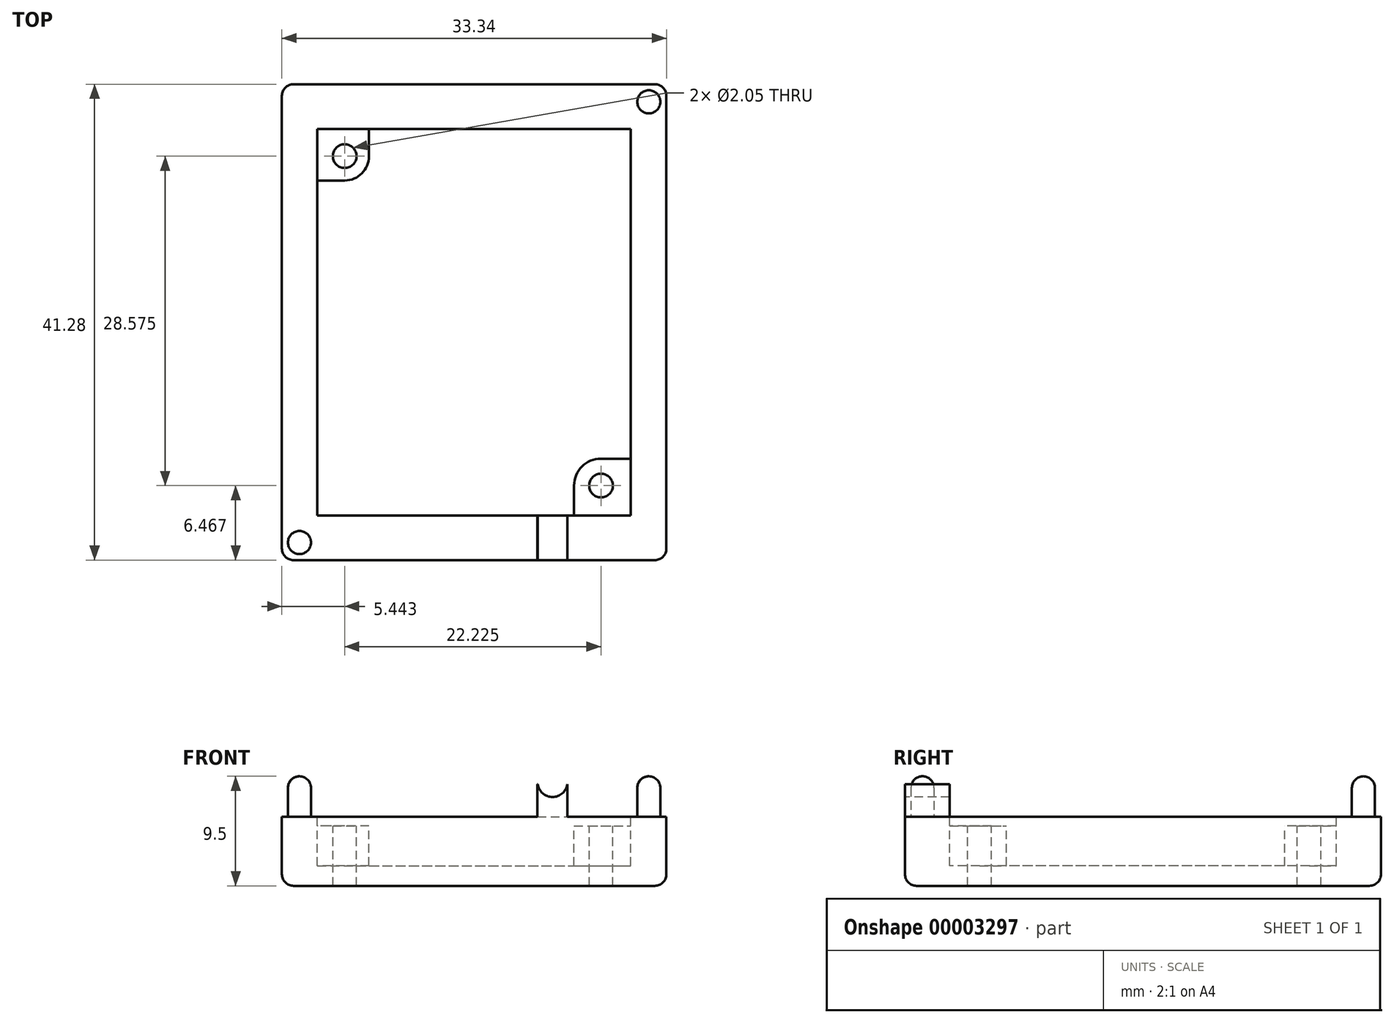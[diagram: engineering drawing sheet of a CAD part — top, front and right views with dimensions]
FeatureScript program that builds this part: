
annotation { "Feature Type Name" : "Feature", "Feature Type Description" : "" }
export const myFeature = defineFeature(function(context is Context, id is Id, definition is map)
    precondition{}
    {
        {
            var Q0;
            Q0=qCreatedBy(makeId("Top.planeOp"),FACE);
            var sketch = newSketch(context, id + "F0", { "sketchPlane" : qUnion([Q0])});
            skLineSegment(sketch, "E0.rect.bottom", {"start": v(16.67, 20.64) * mm, "end": v(-16.67, 20.64) * mm});
            skLineSegment(sketch, "E0.rect.top", {"start": v(16.67, -20.64) * mm, "end": v(-16.67, -20.64) * mm});
            skLineSegment(sketch, "E0.rect.left", {"start": v(16.67, 20.64) * mm, "end": v(16.67, -20.64) * mm});
            skLineSegment(sketch, "E0.rect.right", {"start": v(-16.67, 20.64) * mm, "end": v(-16.67, -20.64) * mm});
            skPoint(sketch, "E0.rect.middle", {"position": v(0, 0) * mm});
            skSolve(sketch);
        }
        {
            var Q0;
            Q0=makeQuery(id+"F0.imprint","IMPRINT",FACE,{"disambiguationData":[TD([[makeQuery(id+"F0.imprint","IMPRINT",EDGE,{"derivedFrom":sQuery(id+"F0.wireOp",EDGE,"E0.rect.bottom")}),1.0]])]});
            extrude(context, id + "F1", {"entities" : qUnion([Q0]), "oppositeDirection" : true, "depth" : 6 * mm});
        }
        {
            var Q0;
            Q0=makeQuery(id+"F1.opExtrude","CAP_FACE",FACE,{"disambiguationData":[OSD([sQuery(id+"F0.wireOp",EDGE,"E0.rect.bottom"),sQuery(id+"F0.wireOp",EDGE,"E0.rect.top"),sQuery(id+"F0.wireOp",EDGE,"E0.rect.left"),sQuery(id+"F0.wireOp",EDGE,"E0.rect.right")])],"isStart":true});
            var sketch = newSketch(context, id + "F2", { "sketchPlane" : qUnion([Q0])});
            skLineSegment(sketch, "E1.rect.bottom", {"start": v(13.33, 16.51) * mm, "end": v(-13.34, 16.51) * mm});
            skLineSegment(sketch, "E1.rect.top", {"start": v(13.34, -16.51) * mm, "end": v(-13.33, -16.51) * mm});
            skLineSegment(sketch, "E1.rect.left", {"start": v(13.33, 16.51) * mm, "end": v(13.34, -16.51) * mm});
            skLineSegment(sketch, "E1.rect.right", {"start": v(-13.34, 16.51) * mm, "end": v(-13.33, -16.51) * mm});
            skPoint(sketch, "E1.rect.middle", {"position": v(0, 0) * mm});
            skCircle(sketch, "E2", {"center": v(11.23, 14.4) * mm, "radius": 1.25 * mm});
            skCircle(sketch, "E3", {"center": v(-11, -14.17) * mm, "radius": 1.25 * mm});
            skCircle(sketch, "E4", {"center": v(11.23, 14.4) * mm, "radius": 2.1 * mm});
            skCircle(sketch, "E5", {"center": v(-11, -14.17) * mm, "radius": 2.34 * mm});
            skLineSegment(sketch, "E6.0", {"start": v(13.59, 16.76) * mm, "end": v(-13.59, 16.76) * mm});
            skLineSegment(sketch, "E6.1", {"start": v(13.59, 16.76) * mm, "end": v(13.59, -16.76) * mm});
            skLineSegment(sketch, "E6.2", {"start": v(13.59, -16.76) * mm, "end": v(-13.59, -16.76) * mm});
            skLineSegment(sketch, "E6.3", {"start": v(-13.59, 16.76) * mm, "end": v(-13.59, -16.76) * mm});
            skLineSegment(sketch, "E7", {"start": v(9.12, 14.4) * mm, "end": v(9.12, 16.76) * mm});
            skLineSegment(sketch, "E8", {"start": v(11.23, 12.3) * mm, "end": v(13.59, 12.3) * mm});
            skLineSegment(sketch, "E9", {"start": v(-11, -11.84) * mm, "end": v(-13.59, -11.84) * mm});
            skLineSegment(sketch, "E10", {"start": v(-8.66, -14.17) * mm, "end": v(-8.66, -16.76) * mm});
            skSolve(sketch);
        }
        {
            var Q0;
            {var subQ6=sQuery(id+"F2.wireOp",EDGE,"E1.rect.right");var subQ10=sQuery(id+"F2.wireOp",EDGE,"E1.rect.bottom");var subQ18=makeQuery(id+"F2.imprint","INTERSECT",VERTEX,{"derivedFrom":[subQ10,subQ6]});Q0=makeQuery(id+"F2.imprint","IMPRINT",FACE,{"disambiguationData":[TD([[makeQuery(id+"F2.imprint","IMPRINT",EDGE,{"disambiguationData":[TD([[subQ18,1.0]])],"derivedFrom":subQ10}),1.0]])]});}
            var Q1;
            {var subQ1=sQuery(id+"F2.wireOp",EDGE,"E1.rect.right");var subQ6=sQuery(id+"F2.wireOp",EDGE,"E1.rect.bottom");var subQ11=makeQuery(id+"F2.imprint","INTERSECT",VERTEX,{"derivedFrom":[subQ6,subQ1]});Q1=makeQuery(id+"F2.imprint","IMPRINT",FACE,{"disambiguationData":[TD([[makeQuery(id+"F2.imprint","IMPRINT",EDGE,{"disambiguationData":[TD([[subQ11,1.0]])],"derivedFrom":subQ6}),-1.0]])]});}
            var Q2;
            {var subQ1=sQuery(id+"F2.wireOp",EDGE,"E1.rect.left");var subQ6=sQuery(id+"F2.wireOp",EDGE,"E1.rect.top");var subQ11=makeQuery(id+"F2.imprint","INTERSECT",VERTEX,{"derivedFrom":[subQ6,subQ1]});Q2=makeQuery(id+"F2.imprint","IMPRINT",FACE,{"disambiguationData":[TD([[makeQuery(id+"F2.imprint","IMPRINT",EDGE,{"disambiguationData":[TD([[subQ11,-1.0]])],"derivedFrom":subQ6}),1.0]])]});}
            extrude(context, id + "F3", {"entities" : qUnion([Q0, Q1, Q2]), "operationType" : NewBodyOperationType.REMOVE, "oppositeDirection" : true, "depth" : 4.26 * mm});
        }
        {
            var Q0;
            Q0=makeQuery(id+"F1.opExtrude","CAP_FACE",FACE,{"disambiguationData":[OSD([sQuery(id+"F0.wireOp",EDGE,"E0.rect.bottom"),sQuery(id+"F0.wireOp",EDGE,"E0.rect.top"),sQuery(id+"F0.wireOp",EDGE,"E0.rect.left"),sQuery(id+"F0.wireOp",EDGE,"E0.rect.right")])],"isStart":true});
            var sketch = newSketch(context, id + "F4", { "sketchPlane" : qUnion([Q0])});
            skLineSegment(sketch, "E11", {"start": v(9.12, 16.76) * mm, "end": v(13.59, 16.76) * mm});
            skLineSegment(sketch, "E12", {"start": v(13.59, 16.76) * mm, "end": v(13.59, 12.3) * mm});
            skLineSegment(sketch, "E13", {"start": v(13.59, 12.3) * mm, "end": v(11.23, 12.3) * mm});
            skArc(sketch, "E14", {"start": v(9.12, 14.4) * mm, "mid": v(9.74, 12.91) * mm, "end": v(11.23, 12.3) * mm});
            skLineSegment(sketch, "E15", {"start": v(9.12, 14.4) * mm, "end": v(9.12, 16.76) * mm});
            skArc(sketch, "E16", {"start": v(-8.66, -14.17) * mm, "mid": v(-9.35, -12.52) * mm, "end": v(-11, -11.84) * mm});
            skLineSegment(sketch, "E17", {"start": v(-8.66, -14.17) * mm, "end": v(-8.66, -16.76) * mm});
            skLineSegment(sketch, "E18", {"start": v(-8.66, -16.76) * mm, "end": v(-13.59, -16.76) * mm});
            skLineSegment(sketch, "E19", {"start": v(-13.59, -16.76) * mm, "end": v(-13.59, -11.84) * mm});
            skLineSegment(sketch, "E20", {"start": v(-13.59, -11.84) * mm, "end": v(-11, -11.84) * mm});
            skSolve(sketch);
        }
        {
            var Q0;
            {Q0=qUnion([makeQuery(id+"F4.imprint","IMPRINT",FACE,{"disambiguationData":[TD([[makeQuery(id+"F4.imprint","IMPRINT",EDGE,{"derivedFrom":sQuery(id+"F4.wireOp",EDGE,"E11")}),-1.0]])]}),makeQuery(id+"F4.imprint","IMPRINT",FACE,{"disambiguationData":[TD([[makeQuery(id+"F4.imprint","IMPRINT",EDGE,{"derivedFrom":sQuery(id+"F4.wireOp",EDGE,"E16")}),1.0]])]})]);}
            extrude(context, id + "F5", {"entities" : qUnion([Q0]), "operationType" : NewBodyOperationType.REMOVE, "oppositeDirection" : true, "depth" : .8 * mm});
        }
        {
            var Q0;
            Q0=makeQuery(id+"F5.boolean.opBoolean","COPY",FACE,{"derivedFrom":makeQuery(id+"F5.opExtrude","CAP_FACE",FACE,{"disambiguationData":[OSD([sQuery(id+"F4.wireOp",EDGE,"E11"),sQuery(id+"F4.wireOp",EDGE,"E12"),sQuery(id+"F4.wireOp",EDGE,"E13"),sQuery(id+"F4.wireOp",EDGE,"E14"),sQuery(id+"F4.wireOp",EDGE,"E15")])],"isStart":false})});
            var sketch = newSketch(context, id + "F6", { "sketchPlane" : qUnion([Q0])});
            skCircle(sketch, "E21", {"center": v(11.23, 14.4) * mm, "radius": 1.02 * mm});
            skSolve(sketch);
        }
        {
            var Q0;
            Q0=makeQuery(id+"F6.imprint","IMPRINT",FACE,{"disambiguationData":[TD([[makeQuery(id+"F6.imprint","IMPRINT",EDGE,{"derivedFrom":sQuery(id+"F6.wireOp",EDGE,"E21")}),1.0]])]});
            extrude(context, id + "F7", {"entities" : qUnion([Q0]), "operationType" : NewBodyOperationType.REMOVE, "oppositeDirection" : true, "depth" : 25.4 * mm});
        }
        {
            var Q0;
            Q0=makeQuery(id+"F5.boolean.opBoolean","COPY",FACE,{"derivedFrom":makeQuery(id+"F5.opExtrude","CAP_FACE",FACE,{"disambiguationData":[OSD([sQuery(id+"F4.wireOp",EDGE,"E16"),sQuery(id+"F4.wireOp",EDGE,"E17"),sQuery(id+"F4.wireOp",EDGE,"E18"),sQuery(id+"F4.wireOp",EDGE,"E19"),sQuery(id+"F4.wireOp",EDGE,"E20")])],"isStart":false})});
            var sketch = newSketch(context, id + "F8", { "sketchPlane" : qUnion([Q0])});
            skCircle(sketch, "E22", {"center": v(-11, -14.17) * mm, "radius": 1.02 * mm});
            skSolve(sketch);
        }
        {
            var Q0;
            Q0=makeQuery(id+"F8.imprint","IMPRINT",FACE,{"disambiguationData":[TD([[makeQuery(id+"F8.imprint","IMPRINT",EDGE,{"derivedFrom":sQuery(id+"F8.wireOp",EDGE,"E22")}),1.0]])]});
            extrude(context, id + "F9", {"entities" : qUnion([Q0]), "operationType" : NewBodyOperationType.REMOVE, "oppositeDirection" : true, "depth" : 25.4 * mm});
        }
        {
            var Q0;
            Q0=makeQuery(id+"F1.opExtrude","CAP_FACE",FACE,{"disambiguationData":[OSD([sQuery(id+"F0.wireOp",EDGE,"E0.rect.bottom"),sQuery(id+"F0.wireOp",EDGE,"E0.rect.top"),sQuery(id+"F0.wireOp",EDGE,"E0.rect.left"),sQuery(id+"F0.wireOp",EDGE,"E0.rect.right")])],"isStart":true});
            var sketch = newSketch(context, id + "F10", { "sketchPlane" : qUnion([Q0])});
            skLineSegment(sketch, "E23.bottom", {"start": v(-13.59, 16.76) * mm, "end": v(-5.09, 16.76) * mm});
            skLineSegment(sketch, "E23.top", {"start": v(-13.59, 20.64) * mm, "end": v(-5.09, 20.64) * mm});
            skLineSegment(sketch, "E23.left", {"start": v(-13.59, 16.76) * mm, "end": v(-13.59, 20.64) * mm});
            skLineSegment(sketch, "E23.right", {"start": v(-5.09, 16.76) * mm, "end": v(-5.09, 20.64) * mm});
            skLineSegment(sketch, "E24.bottom", {"start": v(13.59, -16.76) * mm, "end": v(4.59, -16.76) * mm});
            skLineSegment(sketch, "E24.top", {"start": v(13.59, -20.64) * mm, "end": v(4.59, -20.64) * mm});
            skLineSegment(sketch, "E24.left", {"start": v(13.59, -16.76) * mm, "end": v(13.59, -20.64) * mm});
            skLineSegment(sketch, "E24.right", {"start": v(4.59, -16.76) * mm, "end": v(4.59, -20.64) * mm});
            skSolve(sketch);
        }
        {
            var Q0;
            {Q0=qUnion([makeQuery(id+"F10.imprint","IMPRINT",FACE,{"disambiguationData":[TD([[makeQuery(id+"F10.imprint","IMPRINT",EDGE,{"derivedFrom":sQuery(id+"F10.wireOp",EDGE,"E23.bottom")}),-1.0]])]}),makeQuery(id+"F10.imprint","IMPRINT",FACE,{"disambiguationData":[TD([[makeQuery(id+"F10.imprint","IMPRINT",EDGE,{"derivedFrom":sQuery(id+"F10.wireOp",EDGE,"E24.bottom")}),1.0]])]})]);}
            extrude(context, id + "F11", {"entities" : qUnion([Q0]), "operationType" : NewBodyOperationType.REMOVE, "oppositeDirection" : true, "depth" : .4 * mm});
        }
        {
            var Q0;
            {var subQ0=sQuery(id+"F0.wireOp",EDGE,"E0.rect.bottom");var subQ1=sQuery(id+"F0.wireOp",EDGE,"E0.rect.top");var subQ2=sQuery(id+"F0.wireOp",EDGE,"E0.rect.right");Q0=makeQuery(id+"F11.boolean.opBoolean","SPLIT",FACE,{"disambiguationData":[TD([makeQuery(id+"F1.opExtrude","SWEPT_FACE",FACE,{"disambiguationData":[OSD([subQ2])]})])],"derivedFrom":makeQuery(id+"F1.opExtrude","CAP_FACE",FACE,{"disambiguationData":[OSD([subQ0,subQ1,sQuery(id+"F0.wireOp",EDGE,"E0.rect.left"),subQ2])],"isStart":true})});}
            var sketch = newSketch(context, id + "F12", { "sketchPlane" : qUnion([Q0])});
            skCircle(sketch, "E25", {"center": v(-15.14, 19.11) * mm, "radius": 1 * mm});
            skSolve(sketch);
        }
        {
            var Q0;
            Q0=makeQuery(id+"F12.imprint","IMPRINT",FACE,{"disambiguationData":[TD([[makeQuery(id+"F12.imprint","IMPRINT",EDGE,{"derivedFrom":sQuery(id+"F12.wireOp",EDGE,"E25")}),1.0]])]});
            extrude(context, id + "F13", {"entities" : qUnion([Q0]), "operationType" : NewBodyOperationType.ADD, "depth" : 3.5 * mm});
        }
        {
            var Q0;
            {var subQ0=sQuery(id+"F0.wireOp",EDGE,"E0.rect.bottom");var subQ1=sQuery(id+"F0.wireOp",EDGE,"E0.rect.top");var subQ2=sQuery(id+"F0.wireOp",EDGE,"E0.rect.left");Q0=makeQuery(id+"F11.boolean.opBoolean","SPLIT",FACE,{"disambiguationData":[TD([makeQuery(id+"F1.opExtrude","SWEPT_FACE",FACE,{"disambiguationData":[OSD([subQ2])]})])],"derivedFrom":makeQuery(id+"F1.opExtrude","CAP_FACE",FACE,{"disambiguationData":[OSD([subQ0,subQ1,subQ2,sQuery(id+"F0.wireOp",EDGE,"E0.rect.right")])],"isStart":true})});}
            var sketch = newSketch(context, id + "F14", { "sketchPlane" : qUnion([Q0])});
            skCircle(sketch, "E26", {"center": v(15.14, -19.11) * mm, "radius": 1 * mm});
            skSolve(sketch);
        }
        {
            var Q0;
            Q0=makeQuery(id+"F14.imprint","IMPRINT",FACE,{"disambiguationData":[TD([[makeQuery(id+"F14.imprint","IMPRINT",EDGE,{"derivedFrom":sQuery(id+"F14.wireOp",EDGE,"E26")}),1.0]])]});
            extrude(context, id + "F15", {"entities" : qUnion([Q0]), "operationType" : NewBodyOperationType.ADD, "depth" : 3.5 * mm});
        }
        {
            var Q0;
            Q0=makeQuery(id+"F13.opExtrude","CAP_EDGE",EDGE,{"disambiguationData":[OSD([sQuery(id+"F12.wireOp",EDGE,"E25")])],"isStart":false});
            var Q1;
            Q1=makeQuery(id+"F15.opExtrude","CAP_EDGE",EDGE,{"disambiguationData":[OSD([sQuery(id+"F14.wireOp",EDGE,"E26")])],"isStart":false});
            fillet(context, id + "F16", {"entities" : qUnion([Q0, Q1]), "radius" : 1 * mm, "tangentPropagation" : true, "allowEdgeOverflow" : false});
        }
        {
            var Q0;
            Q0=makeQuery(id+"F1.opExtrude","SWEPT_EDGE",EDGE,{"disambiguationData":[OSD([sQuery(id+"F0.wireOp",EDGE,"E0.rect.bottom"),sQuery(id+"F0.wireOp",EDGE,"E0.rect.left")])]});
            var Q1;
            Q1=makeQuery(id+"F1.opExtrude","SWEPT_EDGE",EDGE,{"disambiguationData":[OSD([sQuery(id+"F0.wireOp",EDGE,"E0.rect.top"),sQuery(id+"F0.wireOp",EDGE,"E0.rect.left")])]});
            var Q2;
            Q2=makeQuery(id+"F1.opExtrude","SWEPT_EDGE",EDGE,{"disambiguationData":[OSD([sQuery(id+"F0.wireOp",EDGE,"E0.rect.top"),sQuery(id+"F0.wireOp",EDGE,"E0.rect.right")])]});
            var Q3;
            Q3=makeQuery(id+"F1.opExtrude","SWEPT_EDGE",EDGE,{"disambiguationData":[OSD([sQuery(id+"F0.wireOp",EDGE,"E0.rect.bottom"),sQuery(id+"F0.wireOp",EDGE,"E0.rect.right")])]});
            var Q4;
            Q4=makeQuery(id+"F1.opExtrude","CAP_EDGE",EDGE,{"disambiguationData":[OSD([sQuery(id+"F0.wireOp",EDGE,"E0.rect.top")])],"isStart":false});
            var Q5;
            Q5=makeQuery(id+"F1.opExtrude","CAP_EDGE",EDGE,{"disambiguationData":[OSD([sQuery(id+"F0.wireOp",EDGE,"E0.rect.left")])],"isStart":false});
            var Q6;
            Q6=makeQuery(id+"F1.opExtrude","CAP_EDGE",EDGE,{"disambiguationData":[OSD([sQuery(id+"F0.wireOp",EDGE,"E0.rect.bottom")])],"isStart":false});
            var Q7;
            Q7=makeQuery(id+"F1.opExtrude","CAP_EDGE",EDGE,{"disambiguationData":[OSD([sQuery(id+"F0.wireOp",EDGE,"E0.rect.right")])],"isStart":false});
            fillet(context, id + "F17", {"entities" : qUnion([Q0, Q1, Q2, Q3, Q4, Q5, Q6, Q7]), "radius" : 1 * mm, "tangentPropagation" : true, "allowEdgeOverflow" : false});
        }
        {
            var Q0;
            Q0=makeQuery(id+"F11.boolean.opBoolean","COPY",FACE,{"derivedFrom":makeQuery(id+"F11.opExtrude","CAP_FACE",FACE,{"disambiguationData":[OSD([sQuery(id+"F10.wireOp",EDGE,"E24.bottom"),sQuery(id+"F10.wireOp",EDGE,"E24.top"),sQuery(id+"F10.wireOp",EDGE,"E24.left"),sQuery(id+"F10.wireOp",EDGE,"E24.right")])],"isStart":false})});
            var sketch = newSketch(context, id + "F18", { "sketchPlane" : qUnion([Q0])});
            skLineSegment(sketch, "E27.bottom", {"start": v(4.59, -16.76) * mm, "end": v(13.59, -16.76) * mm});
            skLineSegment(sketch, "E27.top", {"start": v(4.59, -20.64) * mm, "end": v(13.59, -20.64) * mm});
            skLineSegment(sketch, "E27.left", {"start": v(4.59, -16.76) * mm, "end": v(4.59, -20.64) * mm});
            skLineSegment(sketch, "E27.right", {"start": v(13.59, -16.76) * mm, "end": v(13.59, -20.64) * mm});
            skSolve(sketch);
        }
        {
            var Q0;
            Q0=makeQuery(id+"F18.imprint","IMPRINT",FACE,{"disambiguationData":[TD([[makeQuery(id+"F18.imprint","IMPRINT",EDGE,{"derivedFrom":sQuery(id+"F18.wireOp",EDGE,"E27.bottom")}),1.0]])]});
            extrude(context, id + "F19", {"entities" : qUnion([Q0]), "operationType" : NewBodyOperationType.ADD, "depth" : .4 * mm});
        }
        {
            var Q0;
            Q0=makeQuery(id+"F11.boolean.opBoolean","COPY",FACE,{"derivedFrom":makeQuery(id+"F11.opExtrude","CAP_FACE",FACE,{"disambiguationData":[OSD([sQuery(id+"F10.wireOp",EDGE,"E23.bottom"),sQuery(id+"F10.wireOp",EDGE,"E23.top"),sQuery(id+"F10.wireOp",EDGE,"E23.left"),sQuery(id+"F10.wireOp",EDGE,"E23.right")])],"isStart":false})});
            var sketch = newSketch(context, id + "F20", { "sketchPlane" : qUnion([Q0])});
            skLineSegment(sketch, "E28.bottom", {"start": v(-13.59, 20.64) * mm, "end": v(-5.09, 20.64) * mm});
            skLineSegment(sketch, "E28.top", {"start": v(-13.59, 16.76) * mm, "end": v(-5.09, 16.76) * mm});
            skLineSegment(sketch, "E28.left", {"start": v(-13.59, 20.64) * mm, "end": v(-13.59, 16.76) * mm});
            skLineSegment(sketch, "E28.right", {"start": v(-5.09, 20.64) * mm, "end": v(-5.09, 16.76) * mm});
            skSolve(sketch);
        }
        {
            var Q0;
            Q0=makeQuery(id+"F20.imprint","IMPRINT",FACE,{"disambiguationData":[TD([[makeQuery(id+"F20.imprint","IMPRINT",EDGE,{"derivedFrom":sQuery(id+"F20.wireOp",EDGE,"E28.bottom")}),1.0]])]});
            extrude(context, id + "F21", {"entities" : qUnion([Q0]), "operationType" : NewBodyOperationType.ADD, "depth" : .4 * mm});
        }
        {
            var Q0;
            Q0=qCreatedBy(makeId("Top.planeOp"),FACE);
            var sketch = newSketch(context, id + "F22", { "sketchPlane" : qUnion([Q0])});
            skLineSegment(sketch, "E29", {"start": v(0, 0) * mm, "end": v(0, 40.72) * mm});
            skSolve(sketch);
        }
        {
            var Q0;
            Q0=makeQuery(id+"F1.opExtrude","SWEPT_BODY",BODY,{"disambiguationData":[OSD([sQuery(id+"F0.wireOp",EDGE,"E0.rect.bottom"),sQuery(id+"F0.wireOp",EDGE,"E0.rect.top"),sQuery(id+"F0.wireOp",EDGE,"E0.rect.left"),sQuery(id+"F0.wireOp",EDGE,"E0.rect.right")])]});
            var Q1;
            Q1=sQuery(id+"F22.wireOp",EDGE,"E29");
            transform(context, id + "F23", {"entities" : qUnion([Q0]), "transformType" : TransformType.ROTATION, "transformAxis" : qUnion([Q1]), "angle" : 180 * degree, "makeCopy" : false});
        }
        {
            var Q0;
            Q0=makeQuery(id+"F1.opExtrude","SWEPT_BODY",BODY,{"disambiguationData":[OSD([sQuery(id+"F0.wireOp",EDGE,"E0.rect.bottom"),sQuery(id+"F0.wireOp",EDGE,"E0.rect.top"),sQuery(id+"F0.wireOp",EDGE,"E0.rect.left"),sQuery(id+"F0.wireOp",EDGE,"E0.rect.right")])]});
            var Q1;
            Q1=qCreatedBy(makeId("Top.planeOp"),FACE);
            mirror(context, id + "F24", {"entities" : qUnion([Q0]), "mirrorPlane" : qUnion([Q1])});
        }
        {
            var Q0;
            Q0=makeQuery(id+"F1.opExtrude","SWEPT_BODY",BODY,{"disambiguationData":[OSD([sQuery(id+"F0.wireOp",EDGE,"E0.rect.bottom"),sQuery(id+"F0.wireOp",EDGE,"E0.rect.top"),sQuery(id+"F0.wireOp",EDGE,"E0.rect.left"),sQuery(id+"F0.wireOp",EDGE,"E0.rect.right")])]});
            deleteBodies(context, id + "F25", {"entities" : qUnion([Q0])});
        }
        {
            var Q0;
            {var subQ0=sQuery(id+"F0.wireOp",EDGE,"E0.rect.bottom");var subQ1=sQuery(id+"F0.wireOp",EDGE,"E0.rect.top");var subQ2=sQuery(id+"F0.wireOp",EDGE,"E0.rect.left");var subQ3=sQuery(id+"F0.wireOp",EDGE,"E0.rect.right");var subQ4=makeQuery(id+"F1.opExtrude","CAP_FACE",FACE,{"disambiguationData":[OSD([subQ0,subQ1,subQ2,subQ3])],"isStart":true});Q0=makeQuery(id+"F24.opPattern","COPY",FACE,{"derivedFrom":makeQuery(id+"F21.boolean.opBoolean","MERGE",FACE,{"derivedFrom":[makeQuery(id+"F19.boolean.opBoolean","MERGE",FACE,{"derivedFrom":[makeQuery(id+"F11.boolean.opBoolean","SPLIT",FACE,{"disambiguationData":[TD([makeQuery(id+"F1.opExtrude","SWEPT_FACE",FACE,{"disambiguationData":[OSD([subQ3])]})])],"derivedFrom":subQ4}),makeQuery(id+"F11.boolean.opBoolean","SPLIT",FACE,{"disambiguationData":[TD([makeQuery(id+"F1.opExtrude","SWEPT_FACE",FACE,{"disambiguationData":[OSD([subQ2])]})])],"derivedFrom":subQ4}),makeQuery(id+"F19.opExtrude","CAP_FACE",FACE,{"disambiguationData":[OSD([sQuery(id+"F18.wireOp",EDGE,"E27.bottom"),sQuery(id+"F18.wireOp",EDGE,"E27.top"),sQuery(id+"F18.wireOp",EDGE,"E27.left"),sQuery(id+"F18.wireOp",EDGE,"E27.right")])],"isStart":false})]}),makeQuery(id+"F21.opExtrude","CAP_FACE",FACE,{"disambiguationData":[OSD([sQuery(id+"F20.wireOp",EDGE,"E28.bottom"),sQuery(id+"F20.wireOp",EDGE,"E28.top"),sQuery(id+"F20.wireOp",EDGE,"E28.left"),sQuery(id+"F20.wireOp",EDGE,"E28.right")])],"isStart":false})]}),"instanceName":"1"});}
            var sketch = newSketch(context, id + "F26", { "sketchPlane" : qUnion([Q0])});
            skLineSegment(sketch, "E30.bottom", {"start": v(8.09, -16.76) * mm, "end": v(5.49, -16.76) * mm});
            skLineSegment(sketch, "E30.top", {"start": v(8.09, -20.64) * mm, "end": v(5.49, -20.64) * mm});
            skLineSegment(sketch, "E30.left", {"start": v(8.09, -16.76) * mm, "end": v(8.09, -20.64) * mm});
            skLineSegment(sketch, "E30.right", {"start": v(5.49, -16.76) * mm, "end": v(5.49, -20.64) * mm});
            skSolve(sketch);
        }
        {
            var Q0;
            Q0=makeQuery(id+"F26.imprint","IMPRINT",FACE,{"disambiguationData":[TD([[makeQuery(id+"F26.imprint","IMPRINT",EDGE,{"derivedFrom":sQuery(id+"F26.wireOp",EDGE,"E30.bottom")}),-1.0]])]});
            extrude(context, id + "F27", {"entities" : qUnion([Q0]), "operationType" : NewBodyOperationType.ADD, "depth" : 3 * mm});
        }
        {
            var Q0;
            Q0=makeQuery(id+"F27.boolean.opBoolean","MERGE",FACE,{"derivedFrom":[makeQuery(id+"F24.opPattern","COPY",FACE,{"derivedFrom":makeQuery(id+"F19.boolean.opBoolean","MERGE",FACE,{"derivedFrom":[makeQuery(id+"F1.opExtrude","SWEPT_FACE",FACE,{"disambiguationData":[OSD([sQuery(id+"F0.wireOp",EDGE,"E0.rect.top")])]}),makeQuery(id+"F19.opExtrude","SWEPT_FACE",FACE,{"disambiguationData":[OSD([sQuery(id+"F18.wireOp",EDGE,"E27.top")])]})]}),"instanceName":"1"}),makeQuery(id+"F27.opExtrude","SWEPT_FACE",FACE,{"disambiguationData":[OSD([sQuery(id+"F26.wireOp",EDGE,"E30.top")])]})]});
            var sketch = newSketch(context, id + "F28", { "sketchPlane" : qUnion([Q0])});
            skLineSegment(sketch, "E31", {"start": v(8.09, 0) * mm, "end": v(5.49, 0) * mm});
            skLineSegment(sketch, "E32", {"start": v(6.79, 0) * mm, "end": v(6.79, 3) * mm});
            skCircle(sketch, "E33", {"center": v(6.79, 3) * mm, "radius": 1.3 * mm});
            skLineSegment(sketch, "E34.bottom", {"start": v(5.49, 3) * mm, "end": v(8.09, 3) * mm});
            skLineSegment(sketch, "E34.top", {"start": v(5.49, 2.8) * mm, "end": v(8.09, 2.8) * mm});
            skLineSegment(sketch, "E34.left", {"start": v(5.49, 3) * mm, "end": v(5.49, 2.8) * mm});
            skLineSegment(sketch, "E34.right", {"start": v(8.09, 3) * mm, "end": v(8.09, 2.8) * mm});
            skSolve(sketch);
        }
        {
            var Q0;
            {var subQ3=sQuery(id+"F28.wireOp",EDGE,"E32");var subQ5=sQuery(id+"F28.wireOp",EDGE,"E34.bottom");var subQ7=makeQuery(id+"F28.imprint","INTERSECT",VERTEX,{"derivedFrom":[subQ3,subQ5]});Q0=makeQuery(id+"F28.imprint","IMPRINT",FACE,{"disambiguationData":[TD([[makeQuery(id+"F28.imprint","IMPRINT",EDGE,{"disambiguationData":[TD([[subQ7,1.0]])],"derivedFrom":subQ3}),-1.0]])]});}
            var Q1;
            {var subQ0=sQuery(id+"F28.wireOp",EDGE,"E34.right");Q1=makeQuery(id+"F28.imprint","IMPRINT",FACE,{"disambiguationData":[TD([[makeQuery(id+"F28.imprint","IMPRINT",EDGE,{"derivedFrom":subQ0}),-1.0]])]});}
            var Q2;
            {var subQ1=sQuery(id+"F28.wireOp",EDGE,"E33");var subQ3=sQuery(id+"F28.wireOp",EDGE,"E32");var subQ5=makeQuery(id+"F28.imprint","INTERSECT",VERTEX,{"derivedFrom":[subQ3,subQ1]});Q2=makeQuery(id+"F28.imprint","IMPRINT",FACE,{"disambiguationData":[TD([[makeQuery(id+"F28.imprint","IMPRINT",EDGE,{"disambiguationData":[TD([[subQ5,-1.0]])],"derivedFrom":subQ3}),-1.0]])]});}
            var Q3;
            {var subQ3=sQuery(id+"F28.wireOp",EDGE,"E32");var subQ5=sQuery(id+"F28.wireOp",EDGE,"E34.bottom");var subQ6=makeQuery(id+"F28.imprint","INTERSECT",VERTEX,{"derivedFrom":[subQ3,subQ5]});Q3=makeQuery(id+"F28.imprint","IMPRINT",FACE,{"disambiguationData":[TD([[makeQuery(id+"F28.imprint","IMPRINT",EDGE,{"disambiguationData":[TD([[subQ6,1.0]])],"derivedFrom":subQ3}),1.0]])]});}
            var Q4;
            {var subQ1=sQuery(id+"F28.wireOp",EDGE,"E33");var subQ3=sQuery(id+"F28.wireOp",EDGE,"E32");var subQ5=makeQuery(id+"F28.imprint","INTERSECT",VERTEX,{"derivedFrom":[subQ3,subQ1]});Q4=makeQuery(id+"F28.imprint","IMPRINT",FACE,{"disambiguationData":[TD([[makeQuery(id+"F28.imprint","IMPRINT",EDGE,{"disambiguationData":[TD([[subQ5,-1.0]])],"derivedFrom":subQ3}),1.0]])]});}
            var Q5;
            {var subQ0=sQuery(id+"F28.wireOp",EDGE,"E34.left");Q5=makeQuery(id+"F28.imprint","IMPRINT",FACE,{"disambiguationData":[TD([[makeQuery(id+"F28.imprint","IMPRINT",EDGE,{"derivedFrom":subQ0}),1.0]])]});}
            extrude(context, id + "F29", {"entities" : qUnion([Q0, Q1, Q2, Q3, Q4, Q5]), "operationType" : NewBodyOperationType.REMOVE, "oppositeDirection" : true, "depth" : 25 * mm});
        }
    });
